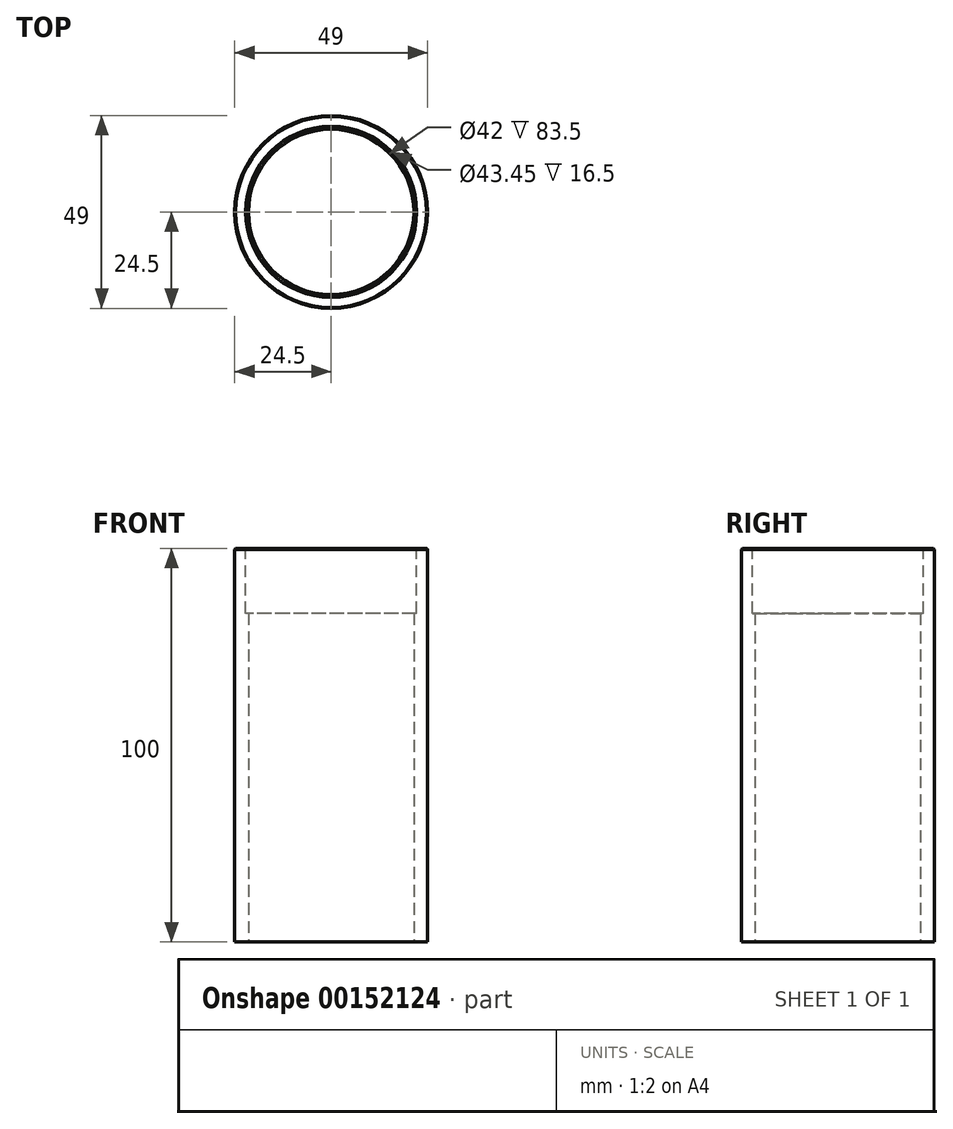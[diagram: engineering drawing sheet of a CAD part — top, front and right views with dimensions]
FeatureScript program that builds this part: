
annotation { "Feature Type Name" : "Feature", "Feature Type Description" : "" }
export const myFeature = defineFeature(function(context is Context, id is Id, definition is map)
    precondition{}
    {
        {
            var Q0;
            Q0=qCreatedBy(makeId("Top.planeOp"),FACE);
            var sketch = newSketch(context, id + "F0", { "sketchPlane" : qUnion([Q0])});
            skCircle(sketch, "E0", {"center": v(0, 0) * mm, "radius": 21 * mm});
            skCircle(sketch, "E1", {"center": v(0, 0) * mm, "radius": 24.5 * mm});
            skSolve(sketch);
        }
        {
            var Q0;
            Q0=makeQuery(id+"F0.imprint","IMPRINT",FACE,{"disambiguationData":[TD([[makeQuery(id+"F0.imprint","IMPRINT",EDGE,{"derivedFrom":sQuery(id+"F0.wireOp",EDGE,"E0")}),-1.0]])]});
            extrude(context, id + "F1", {"entities" : qUnion([Q0]), "depth" : 100 * mm});
        }
        {
            var Q0;
            Q0=makeQuery(id+"F1.opExtrude","CAP_FACE",FACE,{"disambiguationData":[OSD([sQuery(id+"F0.wireOp",EDGE,"E0"),sQuery(id+"F0.wireOp",EDGE,"E1")])],"isStart":false});
            var sketch = newSketch(context, id + "F2", { "sketchPlane" : qUnion([Q0])});
            skCircle(sketch, "E2", {"center": v(0, 0) * mm, "radius": 21.73 * mm});
            skSolve(sketch);
        }
        {
            var Q0;
            Q0=makeQuery(id+"F2.imprint","IMPRINT",FACE,{"disambiguationData":[TD([[makeQuery(id+"F2.imprint","IMPRINT",EDGE,{"derivedFrom":sQuery(id+"F2.wireOp",EDGE,"E2")}),1.0]])]});
            extrude(context, id + "F3", {"entities" : qUnion([Q0]), "operationType" : NewBodyOperationType.REMOVE, "oppositeDirection" : true, "depth" : 16.5 * mm});
        }
        {
            var Q0;
            Q0=makeQuery(id+"F1.opExtrude","CAP_EDGE",EDGE,{"disambiguationData":[OSD([sQuery(id+"F0.wireOp",EDGE,"E1")])],"isStart":false});
            var Q1;
            Q1=makeQuery(id+"F3.boolean.opBoolean","COPY",EDGE,{"derivedFrom":makeQuery(id+"F3.opExtrude","CAP_EDGE",EDGE,{"disambiguationData":[OSD([sQuery(id+"F2.wireOp",EDGE,"E2")])],"isStart":true})});
            chamfer(context, id + "F4", {"entities" : qUnion([Q0, Q1]), "width" : .25 * mm, "tangentPropagation" : true});
        }
    });
